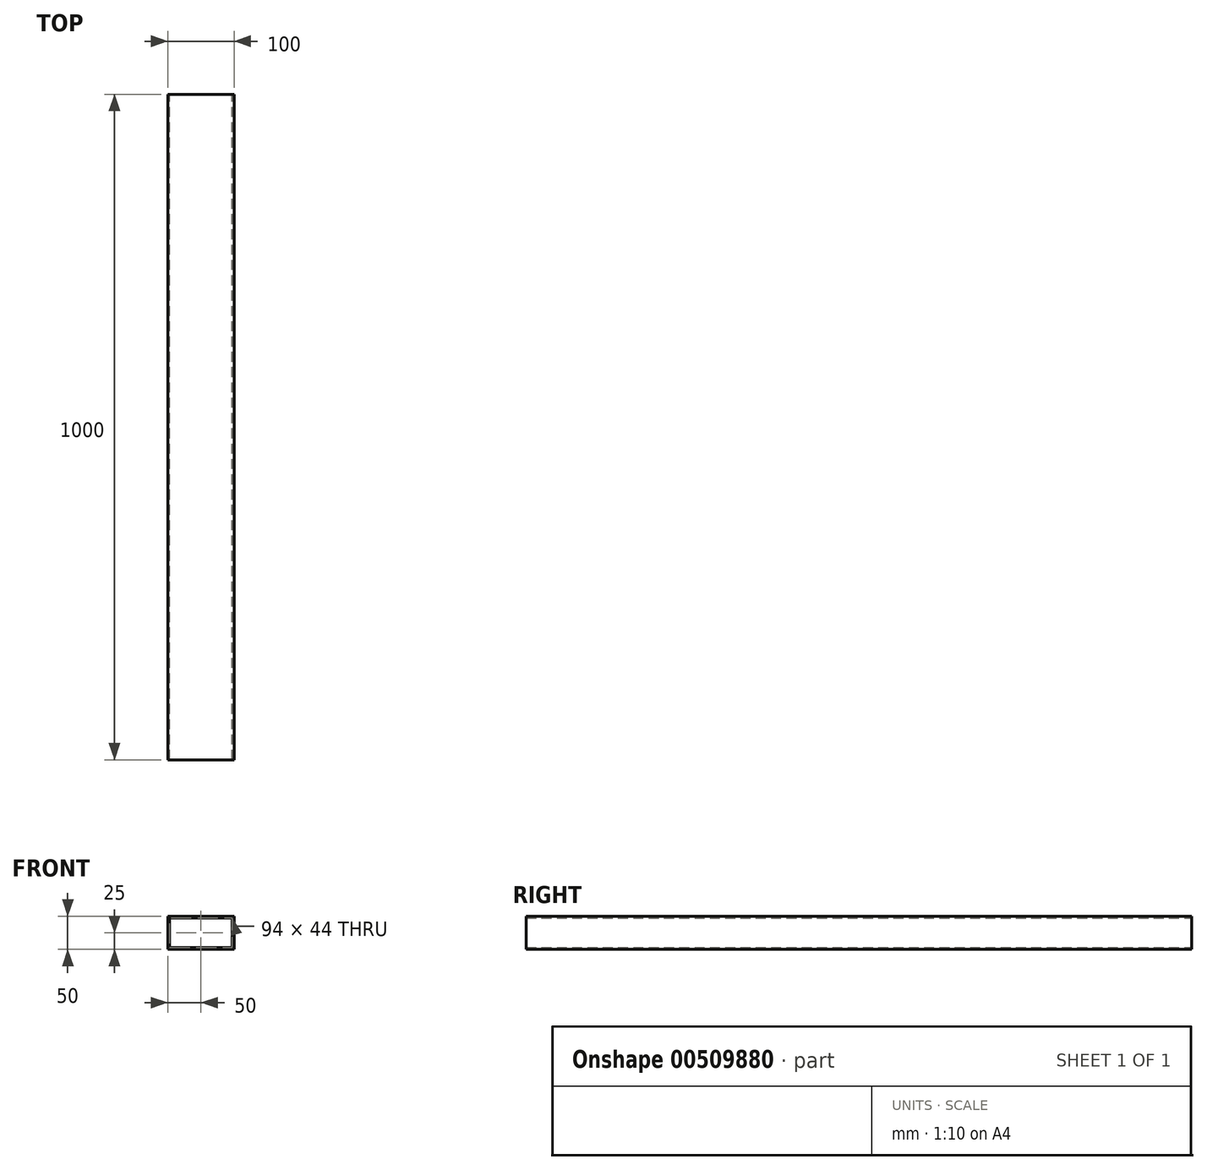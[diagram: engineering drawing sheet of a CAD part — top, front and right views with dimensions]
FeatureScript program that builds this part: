
annotation { "Feature Type Name" : "Feature", "Feature Type Description" : "" }
export const myFeature = defineFeature(function(context is Context, id is Id, definition is map)
    precondition{}
    {
        {
            var Q0;
            Q0=qCreatedBy(makeId("Front.planeOp"),FACE);
            var sketch = newSketch(context, id + "F0", { "sketchPlane" : qUnion([Q0])});
            skLineSegment(sketch, "E0.bottom", {"start": v(50, -25) * mm, "end": v(-50, -25) * mm});
            skLineSegment(sketch, "E0.top", {"start": v(50, 25) * mm, "end": v(-50, 25) * mm});
            skLineSegment(sketch, "E0.left", {"start": v(50, -25) * mm, "end": v(50, 25) * mm});
            skLineSegment(sketch, "E0.right", {"start": v(-50, -25) * mm, "end": v(-50, 25) * mm});
            skPoint(sketch, "E0.middle", {"position": v(0, 0) * mm});
            skLineSegment(sketch, "E1.bottom", {"start": v(47, -22) * mm, "end": v(-47, -22) * mm});
            skLineSegment(sketch, "E1.top", {"start": v(47, 22) * mm, "end": v(-47, 22) * mm});
            skLineSegment(sketch, "E1.left", {"start": v(47, -22) * mm, "end": v(47, 22) * mm});
            skLineSegment(sketch, "E1.right", {"start": v(-47, -22) * mm, "end": v(-47, 22) * mm});
            skSolve(sketch);
        }
        {
            var Q0;
            Q0=makeQuery(id+"F0.imprint","IMPRINT",FACE,{"disambiguationData":[TD([[makeQuery(id+"F0.imprint","IMPRINT",EDGE,{"derivedFrom":sQuery(id+"F0.wireOp",EDGE,"E0.bottom")}),-1.0]])]});
            extrude(context, id + "F1", {"entities" : qUnion([Q0]), "depth" : 1000 * mm, "offsetDistance" : 25 * mm});
        }
    });
